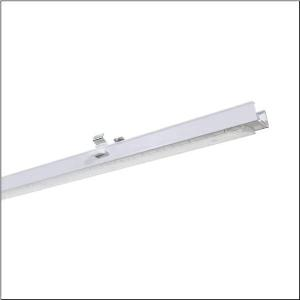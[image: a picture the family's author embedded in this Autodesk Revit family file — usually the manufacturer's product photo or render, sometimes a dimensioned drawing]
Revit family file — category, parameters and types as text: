
# Revit family: trunking_flex_31_51re14mb68b
name_source: partatom
category: Lighting Fixtures
units: mm (PartAtom-declared; Revit-internal decimal feet)

## family parameters
Cut with Voids When Loaded = No
Host = Face
Light Source = No
Part Type = Normal
Room Calculation Point = No
Round Connector Dimension = Use Diameter
Shared = No

## types (1)
- --- (1 x LED, 8000 lm, 50 W, 6500K)
    Apparent Load = 50 VA
    CIE Flux Codes = 72 92 98 99 100
    Color Rendering = 80
    Color Temperature = 6500K
    Default Elevation = 1800 mm
    Description = Trunking Flex 31, luminaire insert, of extruded aluminium section, coated, traffic white (RAL 9016), length: 1.472mm, width: 91mm, height: 53mm, LED rated luminous flux: 8.000lm, light colour: 865, control gear: ON/OFF Multilumen, with system connector: socket, mains connection: 220..240V, AC, 50/60Hz, rated input power: 50W, luminous flux adjustable on luminaire in four steps (4130/5610/6850/8000lm), connected load according to luminous flux setting (25/34/42/50W), primary light control with lens, of plastic, primary optical cover: cover, of PMMA, light emission: direct distribution, primary light characteristic: asymmetric, protection rating (complete): IP20, insulation class (complete): insulation class I (protective earthing), certification: CE, UKCA, impact resistance: IK02, permissible ambient temperature for indoor applications: -20..+40°C, packaging unit: 1 piece
    Height = 58 mm
    Lamp = 1 x LED
    Lamp Light Flux = 8000 lm
    Lamp Power = 50 W
    Lamp count = 1
    Length = 1472 mm
    Luminous efficacy = 160 lm/W
    Manufacturer = Siteco
    ModVariant = No
    Model = 51RE14MB68B
    Mounting Place = Ceiling
    Mounting Type = Pendant
    Number of Poles = 1
    OnlyDefault = Yes
    Power Factor = 1
    Product Name = Trunking Flex 31
    Product group = luminaire insert
    ProductGroupID = 901
    Protection Class = Protection class I
    Protection Degree = IP 20
    RLX_Detail_Level = 1
    RLX_Emergency_Light_Flux = 0 lm
    RLX_Emergency_Type = 0
    RLX_Emergency_Type_DB = No
    RlxData = <blob elided: 21061 chars, md5=156acab6>
    Socket = socket
    Standby Power = 0 W
    System Light Flux = 8000 lm
    System Power = 50 W
    Type Comments = factory setting: luminous flux: 100 % | (ON | ON) | 300 mA
    Type Image = l_1266702.jpg
    URL = http://relux.com
    VarID = @adj_027211
    Voltage = 0 V
    Weight = 0.00 kg
    Width = 65 mm

## geometry (parser evidence)
native form markers: Blend x4, Sweep x9
no freeform markers — native parametric forms only
